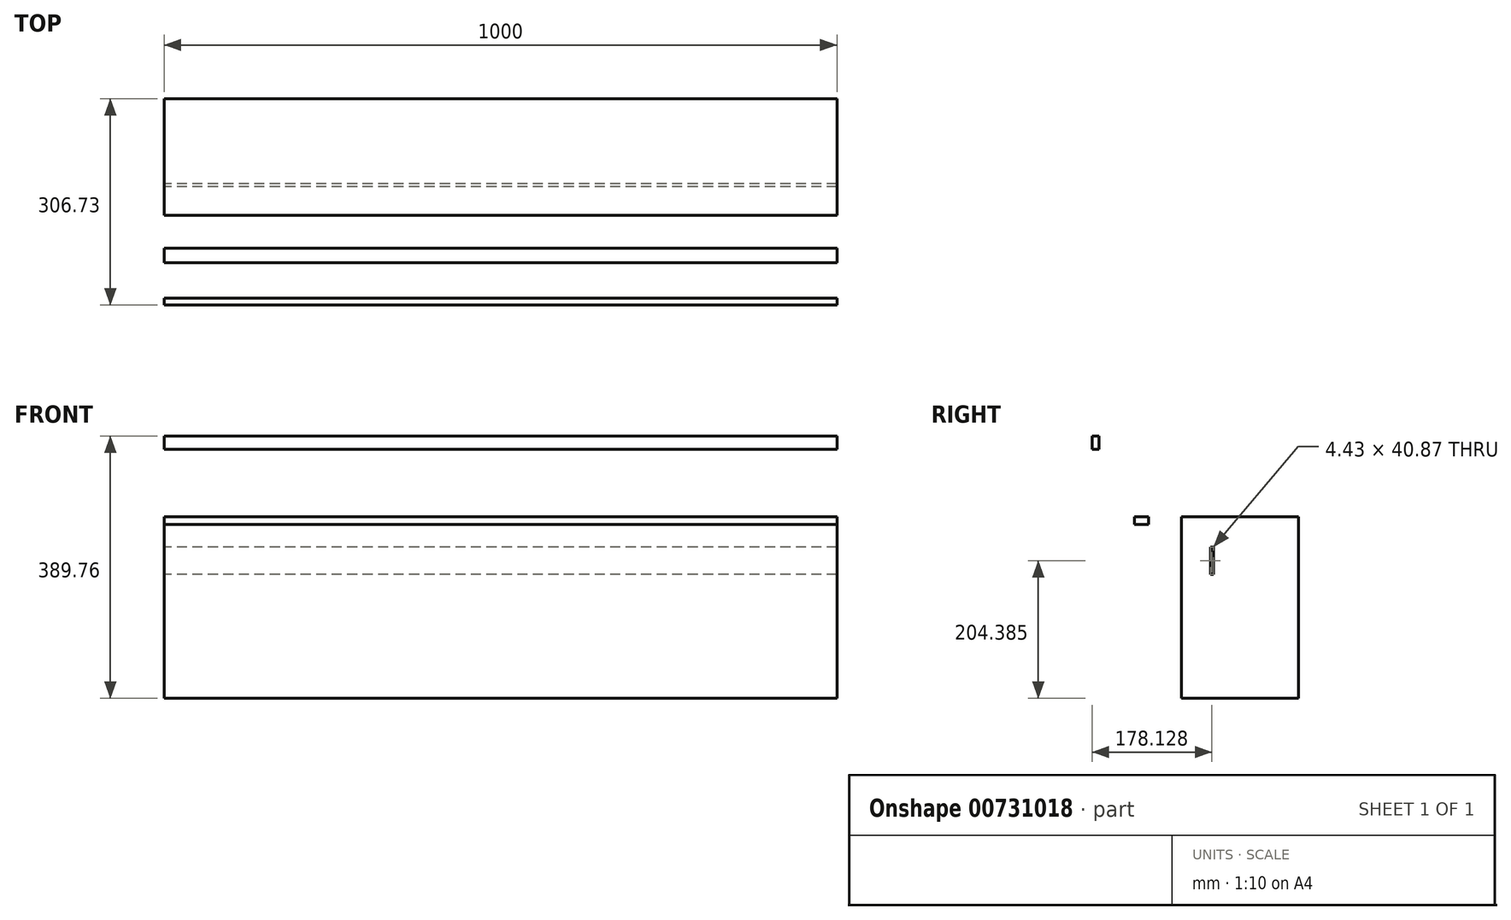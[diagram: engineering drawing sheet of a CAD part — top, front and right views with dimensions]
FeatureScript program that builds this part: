
annotation { "Feature Type Name" : "Feature", "Feature Type Description" : "" }
export const myFeature = defineFeature(function(context is Context, id is Id, definition is map)
    precondition{}
    {
        {
            var Q0;
            Q0=qCreatedBy(makeId("Right.planeOp"),FACE);
            var sketch = newSketch(context, id + "F0", { "sketchPlane" : qUnion([Q0])});
            skLineSegment(sketch, "E0.bottom", {"start": v(-151.52, 164.94) * mm, "end": v(-141.17, 164.94) * mm});
            skLineSegment(sketch, "E0.top", {"start": v(-151.52, 145.26) * mm, "end": v(-141.17, 145.26) * mm});
            skLineSegment(sketch, "E0.left", {"start": v(-151.52, 164.94) * mm, "end": v(-151.52, 145.26) * mm});
            skLineSegment(sketch, "E0.right", {"start": v(-141.17, 164.94) * mm, "end": v(-141.17, 145.26) * mm});
            skLineSegment(sketch, "E1.bottom", {"start": v(24.4, 0) * mm, "end": v(28.82, 0) * mm});
            skLineSegment(sketch, "E1.top", {"start": v(24.4, -40.87) * mm, "end": v(28.82, -40.87) * mm});
            skLineSegment(sketch, "E1.left", {"start": v(24.4, 0) * mm, "end": v(24.4, -40.87) * mm});
            skLineSegment(sketch, "E1.right", {"start": v(28.82, 0) * mm, "end": v(28.82, -40.87) * mm});
            skLineSegment(sketch, "E2.bottom", {"start": v(-18.48, -16.36) * mm, "end": v(0, -16.36) * mm});
            skLineSegment(sketch, "E2.top", {"start": v(-18.48, -161.33) * mm, "end": v(0, -161.33) * mm});
            skLineSegment(sketch, "E2.left", {"start": v(-18.48, -16.36) * mm, "end": v(-18.48, -161.33) * mm});
            skLineSegment(sketch, "E2.right", {"start": v(0, -16.36) * mm, "end": v(0, -161.33) * mm});
            skLineSegment(sketch, "E3.bottom", {"start": v(-67.26, 45.15) * mm, "end": v(-88.7, 45.15) * mm});
            skLineSegment(sketch, "E3.top", {"start": v(-67.26, 33.25) * mm, "end": v(-88.7, 33.25) * mm});
            skLineSegment(sketch, "E3.left", {"start": v(-67.26, 45.15) * mm, "end": v(-67.26, 33.25) * mm});
            skLineSegment(sketch, "E3.right", {"start": v(-88.7, 45.15) * mm, "end": v(-88.7, 33.25) * mm});
            skPoint(sketch, "E4.firstSnap0", {"position": v(-18.48, -88.85) * mm});
            skLineSegment(sketch, "E4.bottom", {"start": v(-18.48, 45.15) * mm, "end": v(155.21, 45.15) * mm});
            skLineSegment(sketch, "E4.top", {"start": v(-18.48, -224.82) * mm, "end": v(155.21, -224.82) * mm});
            skLineSegment(sketch, "E4.left", {"start": v(-18.48, 45.15) * mm, "end": v(-18.48, -224.82) * mm});
            skLineSegment(sketch, "E4.right", {"start": v(155.21, 45.15) * mm, "end": v(155.21, -224.82) * mm});
            skSolve(sketch);
        }
        {
            var Q0;
            Q0 = qSketchRegion(id + "F0", true);
            extrude(context, id + "F1", {"entities" : qUnion([Q0]), "depth" : 1000 * mm, "offsetDistance" : 25.4 * mm});
        }
    });
